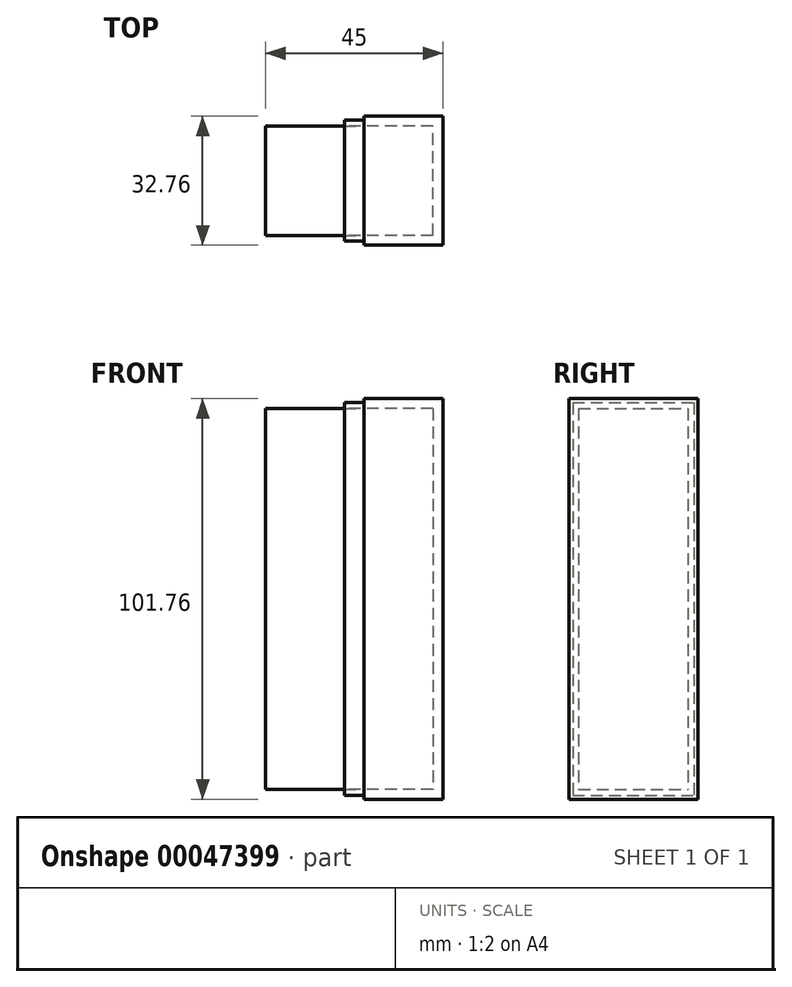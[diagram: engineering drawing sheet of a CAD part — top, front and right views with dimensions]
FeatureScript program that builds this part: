
annotation { "Feature Type Name" : "Feature", "Feature Type Description" : "" }
export const myFeature = defineFeature(function(context is Context, id is Id, definition is map)
    precondition{}
    {
        {
            var Q0;
            Q0=qCreatedBy(makeId("Front.planeOp"),FACE);
            var sketch = newSketch(context, id + "F0", { "sketchPlane" : qUnion([Q0])});
            skLineSegment(sketch, "E0", {"start": v(0, 5) * mm, "end": v(50, 5) * mm});
            skLineSegment(sketch, "E1", {"start": v(50, 5) * mm, "end": v(50, 0) * mm});
            skLineSegment(sketch, "E2", {"start": v(50, 0) * mm, "end": v(0, 0) * mm});
            skLineSegment(sketch, "E3", {"start": v(0, 0) * mm, "end": v(0, 5) * mm});
            skSolve(sketch);
        }
        {
            var Q0;
            Q0=makeQuery(id+"F0.imprint","IMPRINT",FACE,{"disambiguationData":[TD([[makeQuery(id+"F0.imprint","IMPRINT",EDGE,{"derivedFrom":sQuery(id+"F0.wireOp",EDGE,"E0")}),-1.0]])]});
            var Q1;
            Q1=sQuery(id+"F0.wireOp",EDGE,"E2");
            revolve(context, id + "F1", {"entities" : qUnion([Q0]), "axis" : qUnion([Q1]), "revolveType" : RevolveType.FULL});
        }
        {
            var Q0;
            Q0=makeQuery(id+"F1.opRevolve","SWEPT_EDGE",EDGE,{"disambiguationData":[OSD([sQuery(id+"F0.wireOp",EDGE,"E0"),sQuery(id+"F0.wireOp",EDGE,"E1")])]});
            var Q1;
            Q1=makeQuery(id+"F1.opRevolve","SWEPT_EDGE",EDGE,{"disambiguationData":[OSD([sQuery(id+"F0.wireOp",EDGE,"E0"),sQuery(id+"F0.wireOp",EDGE,"E3")])]});
            chamfer(context, id + "F2", {"entities" : qUnion([Q0, Q1]), "chamferType" : ChamferType.OFFSET_ANGLE, "width" : 1 * mm, "oppositeDirection" : false, "angle" : 45 * degree, "tangentPropagation" : true});
        }
        {
            var Q0;
            Q0=qCreatedBy(makeId("Right.planeOp"),FACE);
            var sketch = newSketch(context, id + "F3", { "sketchPlane" : qUnion([Q0])});
            skLineSegment(sketch, "E4.bottom", {"start": v(-44.93, 52.37) * mm, "end": v(-12.17, 52.37) * mm});
            skLineSegment(sketch, "E4.top", {"start": v(-44.93, -49.4) * mm, "end": v(-12.17, -49.4) * mm});
            skLineSegment(sketch, "E4.left", {"start": v(-44.93, 52.37) * mm, "end": v(-44.93, -49.4) * mm});
            skLineSegment(sketch, "E4.right", {"start": v(-12.17, 52.37) * mm, "end": v(-12.17, -49.4) * mm});
            skSolve(sketch);
        }
        {
            var Q0;
            Q0=makeQuery(id+"F3.imprint","IMPRINT",FACE,{"disambiguationData":[TD([[makeQuery(id+"F3.imprint","IMPRINT",EDGE,{"derivedFrom":sQuery(id+"F3.wireOp",EDGE,"E4.bottom")}),-1.0]])]});
            extrude(context, id + "F4", {"entities" : qUnion([Q0]), "depth" : 25 * mm});
        }
        {
            var Q0;
            Q0=makeQuery(id+"F4.opExtrude","CAP_FACE",FACE,{"disambiguationData":[OSD([sQuery(id+"F3.wireOp",EDGE,"E4.bottom"),sQuery(id+"F3.wireOp",EDGE,"E4.top"),sQuery(id+"F3.wireOp",EDGE,"E4.left"),sQuery(id+"F3.wireOp",EDGE,"E4.right")])],"isStart":true});
            shell(context, id + "F5", {"entities" : qUnion([Q0]), "thickness" : 2.5 * mm});
        }
        {
            var Q0;
            Q0=makeQuery(id+"F4.opExtrude","CAP_FACE",FACE,{"disambiguationData":[OSD([sQuery(id+"F3.wireOp",EDGE,"E4.bottom"),sQuery(id+"F3.wireOp",EDGE,"E4.top"),sQuery(id+"F3.wireOp",EDGE,"E4.left"),sQuery(id+"F3.wireOp",EDGE,"E4.right")])],"isStart":true});
            var sketch = newSketch(context, id + "F6", { "sketchPlane" : qUnion([Q0])});
            skLineSegment(sketch, "E5.0", {"start": v(43.93, 51.37) * mm, "end": v(43.93, -48.4) * mm});
            skLineSegment(sketch, "E5.1", {"start": v(43.93, 51.37) * mm, "end": v(13.17, 51.37) * mm});
            skLineSegment(sketch, "E5.2", {"start": v(13.17, 51.37) * mm, "end": v(13.17, -48.4) * mm});
            skLineSegment(sketch, "E5.3", {"start": v(43.93, -48.4) * mm, "end": v(13.17, -48.4) * mm});
            skSolve(sketch);
        }
        {
            var Q0;
            Q0=makeQuery(id+"F6.imprint","IMPRINT",FACE,{"disambiguationData":[TD([[makeQuery(id+"F6.imprint","IMPRINT",EDGE,{"derivedFrom":sQuery(id+"F6.wireOp",EDGE,"E5.0")}),1.0]])]});
            extrude(context, id + "F7", {"entities" : qUnion([Q0]), "operationType" : NewBodyOperationType.REMOVE, "oppositeDirection" : true, "depth" : 5 * mm});
        }
        {
            var Q0;
            Q0=makeQuery(id+"F7.boolean.opBoolean","COPY",FACE,{"derivedFrom":makeQuery(id+"F7.opExtrude","CAP_FACE",FACE,{"disambiguationData":[OSD([sQuery(id+"F3.wireOp",EDGE,"E4.bottom"),sQuery(id+"F3.wireOp",EDGE,"E4.top"),sQuery(id+"F3.wireOp",EDGE,"E4.left"),sQuery(id+"F3.wireOp",EDGE,"E4.right"),sQuery(id+"F6.wireOp",EDGE,"E5.0"),sQuery(id+"F6.wireOp",EDGE,"E5.1"),sQuery(id+"F6.wireOp",EDGE,"E5.2"),sQuery(id+"F6.wireOp",EDGE,"E5.3")])],"isStart":false})});
            var sketch = newSketch(context, id + "F8", { "sketchPlane" : qUnion([Q0])});
            skLineSegment(sketch, "E6.0", {"start": v(44.93, 52.37) * mm, "end": v(12.17, 52.37) * mm});
            skLineSegment(sketch, "E7.0", {"start": v(44.93, 52.37) * mm, "end": v(44.93, -49.4) * mm});
            skLineSegment(sketch, "E8.0", {"start": v(42.43, 49.87) * mm, "end": v(14.67, 49.87) * mm});
            skLineSegment(sketch, "E9.0", {"start": v(42.43, 49.87) * mm, "end": v(42.43, -46.9) * mm});
            skLineSegment(sketch, "E10.0", {"start": v(14.67, 49.87) * mm, "end": v(14.67, -46.9) * mm});
            skLineSegment(sketch, "E11.0", {"start": v(13.17, 51.37) * mm, "end": v(13.17, -48.4) * mm});
            skLineSegment(sketch, "E12.0", {"start": v(42.43, -46.9) * mm, "end": v(14.67, -46.9) * mm});
            skLineSegment(sketch, "E13.0", {"start": v(44.93, -49.4) * mm, "end": v(12.17, -49.4) * mm});
            skPoint(sketch, "E14.0.end.orphan", {"position": v(43.93, -48.4) * mm});
            skPoint(sketch, "E14.0.start.orphan", {"position": v(43.93, 51.37) * mm});
            skSolve(sketch);
        }
        {
            var Q0;
            Q0 = qSketchRegion(id + "F8", true);
            extrude(context, id + "F9", {"entities" : qUnion([Q0]), "depth" : 25 * mm});
        }
        {
            var Q0;
            Q0=makeQuery(id+"F1.opRevolve","SWEPT_BODY",BODY,{"disambiguationData":[OSD([sQuery(id+"F0.wireOp",EDGE,"E0"),sQuery(id+"F0.wireOp",EDGE,"E1"),sQuery(id+"F0.wireOp",EDGE,"E2"),sQuery(id+"F0.wireOp",EDGE,"E3")])]});
            deleteBodies(context, id + "F10", {"entities" : qUnion([Q0])});
        }
    });
